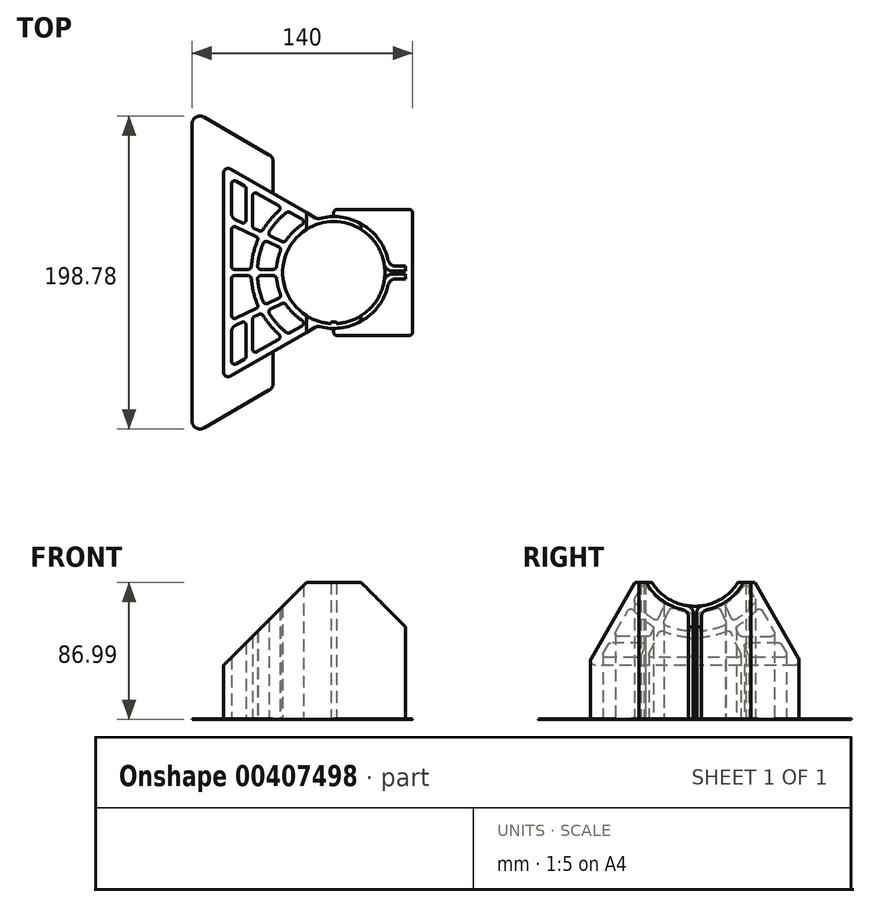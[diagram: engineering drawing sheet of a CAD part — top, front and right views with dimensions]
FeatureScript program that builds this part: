
annotation { "Feature Type Name" : "Feature", "Feature Type Description" : "" }
export const myFeature = defineFeature(function(context is Context, id is Id, definition is map)
    precondition{}
    {
        {
            var Q0;
            Q0=qCreatedBy(makeId("Top.planeOp"),FACE);
            var sketch = newSketch(context, id + "F0", { "sketchPlane" : qUnion([Q0])});
            skArc(sketch, "E0", {"start": v(32.08, 5.2) * mm, "mid": v(-24.03, 21.88) * mm, "end": v(-2.18, -32.43) * mm});
            skArc(sketch, "E1", {"start": v(34.61, 7.89) * mm, "mid": v(18.34, 30.4) * mm, "end": v(-9.16, 34.3) * mm});
            skLineSegment(sketch, "E2", {"start": v(39.49, 4) * mm, "end": v(45.5, 4) * mm});
            skLineSegment(sketch, "E3", {"start": v(39.49, -4) * mm, "end": v(45.5, -4) * mm});
            skLineSegment(sketch, "E4.0", {"start": v(37.02, 1) * mm, "end": v(45.5, 1) * mm});
            skLineSegment(sketch, "E5.0", {"start": v(37.02, -1) * mm, "end": v(45.5, -1) * mm});
            skLineSegment(sketch, "E6", {"start": v(45.5, 4) * mm, "end": v(45.5, 1) * mm});
            skLineSegment(sketch, "E7.trimOffspring", {"start": v(45.5, -1) * mm, "end": v(45.5, -4) * mm});
            skPoint(sketch, "E8.visualSharp", {"position": v(35.27, 4) * mm});
            skArc(sketch, "E8.filletArc", {"start": v(34.61, 7.89) * mm, "mid": v(36.37, 5.1) * mm, "end": v(39.49, 4) * mm});
            skPoint(sketch, "E9.visualSharp", {"position": v(35.27, -4) * mm});
            skArc(sketch, "E9.filletArc", {"start": v(39.49, -4) * mm, "mid": v(36.37, -5.1) * mm, "end": v(34.61, -7.89) * mm});
            skPoint(sketch, "E10.visualSharp", {"position": v(32.48, -1) * mm});
            skArc(sketch, "E10.filletArc", {"start": v(37.02, -1) * mm, "mid": v(33.78, -2.2) * mm, "end": v(32.08, -5.2) * mm});
            skPoint(sketch, "E11.visualSharp", {"position": v(32.48, 1) * mm});
            skArc(sketch, "E11.filletArc", {"start": v(32.08, 5.2) * mm, "mid": v(33.78, 2.2) * mm, "end": v(37.02, 1) * mm});
            skArc(sketch, "E12.trimOffspring", {"start": v(-9.16, -34.3) * mm, "mid": v(18.34, -30.4) * mm, "end": v(34.61, -7.89) * mm});
            skLineSegment(sketch, "E13", {"start": v(-11.44, 34.6) * mm, "end": v(-65.5, 65.81) * mm});
            skLineSegment(sketch, "E14", {"start": v(-11.44, -34.6) * mm, "end": v(-65.5, -65.81) * mm});
            skLineSegment(sketch, "E15", {"start": v(-70, 63.21) * mm, "end": v(-70, -63.21) * mm});
            skPoint(sketch, "E16.visualSharp", {"position": v(-70, 68.4) * mm});
            skArc(sketch, "E16.filletArc", {"start": v(-65.5, 65.81) * mm, "mid": v(-68.5, 65.81) * mm, "end": v(-70, 63.21) * mm});
            skPoint(sketch, "E17.visualSharp", {"position": v(-70, -68.4) * mm});
            skArc(sketch, "E17.filletArc", {"start": v(-70, -63.21) * mm, "mid": v(-68.5, -65.81) * mm, "end": v(-65.5, -65.81) * mm});
            skPoint(sketch, "E18.visualSharp", {"position": v(-10.34, 33.96) * mm});
            skArc(sketch, "E18.filletArc", {"start": v(-11.44, 34.6) * mm, "mid": v(-10.33, 34.22) * mm, "end": v(-9.16, 34.3) * mm});
            skPoint(sketch, "E19.visualSharp", {"position": v(-10.34, -33.96) * mm});
            skArc(sketch, "E19.filletArc", {"start": v(-9.16, -34.3) * mm, "mid": v(-10.33, -34.22) * mm, "end": v(-11.44, -34.6) * mm});
            skLineSegment(sketch, "E20.bottom", {"start": v(-1.35, -31.5) * mm, "end": v(1.35, -31.5) * mm});
            skLineSegment(sketch, "E20.left", {"start": v(-1.75, -31.9) * mm, "end": v(-1.75, -32.03) * mm});
            skLineSegment(sketch, "E20.right", {"start": v(1.75, -31.9) * mm, "end": v(1.75, -32.03) * mm});
            skArc(sketch, "E21.trimOffspring", {"start": v(2.18, -32.43) * mm, "mid": v(21.88, -24.03) * mm, "end": v(32.08, -5.2) * mm});
            skPoint(sketch, "E20.top.end.orphan", {"position": v(1.75, -33.96) * mm});
            skPoint(sketch, "E22.visualSharp", {"position": v(-1.75, -31.5) * mm});
            skArc(sketch, "E22.filletArc", {"start": v(-1.35, -31.5) * mm, "mid": v(-1.63, -31.62) * mm, "end": v(-1.75, -31.9) * mm});
            skPoint(sketch, "E23.visualSharp", {"position": v(1.75, -31.5) * mm});
            skArc(sketch, "E23.filletArc", {"start": v(1.75, -31.9) * mm, "mid": v(1.63, -31.62) * mm, "end": v(1.35, -31.5) * mm});
            skPoint(sketch, "E24.visualSharp", {"position": v(-1.75, -32.45) * mm});
            skArc(sketch, "E24.filletArc", {"start": v(-2.18, -32.43) * mm, "mid": v(-1.88, -32.32) * mm, "end": v(-1.75, -32.03) * mm});
            skPoint(sketch, "E25.visualSharp", {"position": v(1.75, -32.45) * mm});
            skArc(sketch, "E25.filletArc", {"start": v(1.75, -32.03) * mm, "mid": v(1.88, -32.32) * mm, "end": v(2.18, -32.43) * mm});
            skSolve(sketch);
        }
        {
            var Q0;
            Q0 = qSketchRegion(id + "F0", true);
            extrude(context, id + "F1", {"entities" : qUnion([Q0]), "depth" : 150 * mm});
        }
        {
            var Q0;
            Q0=qCreatedBy(makeId("Front.planeOp"),FACE);
            var sketch = newSketch(context, id + "F2", { "sketchPlane" : qUnion([Q0])});
            skLineSegment(sketch, "E26", {"start": v(-17.41, 86.99) * mm, "end": v(-77.36, 27.04) * mm});
            skLineSegment(sketch, "E27", {"start": v(50.55, 154.95) * mm, "end": v(-77.36, 154.95) * mm});
            skLineSegment(sketch, "E28", {"start": v(-77.36, 27.04) * mm, "end": v(-77.36, 154.95) * mm});
            skLineSegment(sketch, "E29", {"start": v(0, -24.5) * mm, "end": v(0, 134.81) * mm, "construction": true});
            skLineSegment(sketch, "E30", {"start": v(17.41, 86.99) * mm, "end": v(50.55, 53.86) * mm});
            skLineSegment(sketch, "E31", {"start": v(50.55, 154.95) * mm, "end": v(50.55, 53.86) * mm});
            skPoint(sketch, "E32.startSnap0", {"position": v(-77.36, 91) * mm});
            skPoint(sketch, "E33.orphan", {"position": v(-42.6, 91) * mm});
            skLineSegment(sketch, "E34", {"start": v(17.41, 86.99) * mm, "end": v(-17.41, 86.99) * mm});
            skSolve(sketch);
        }
        {
            var Q0;
            Q0 = qSketchRegion(id + "F2", true);
            extrude(context, id + "F3", {"entities" : qUnion([Q0]), "operationType" : NewBodyOperationType.REMOVE, "endBound" : BoundingType.SYMMETRIC, "oppositeDirection" : true, "depth" : 150 * mm});
        }
        {
            var Q0;
            Q0=qCreatedBy(makeId("Top.planeOp"),FACE);
            var sketch = newSketch(context, id + "F4", { "sketchPlane" : qUnion([Q0])});
            skLineSegment(sketch, "E35.bottom", {"start": v(2, -40) * mm, "end": v(48, -40) * mm});
            skLineSegment(sketch, "E35.top", {"start": v(2, 40) * mm, "end": v(48, 40) * mm});
            skLineSegment(sketch, "E35.left", {"start": v(0, -38) * mm, "end": v(0, -32.5) * mm});
            skLineSegment(sketch, "E35.right", {"start": v(50, -38) * mm, "end": v(50, 38) * mm});
            skPoint(sketch, "E36.visualSharp", {"position": v(0, -40) * mm});
            skArc(sketch, "E36.filletArc", {"start": v(0, -38) * mm, "mid": v(0.59, -39.41) * mm, "end": v(2, -40) * mm});
            skPoint(sketch, "E37.visualSharp", {"position": v(50, -40) * mm});
            skArc(sketch, "E37.filletArc", {"start": v(48, -40) * mm, "mid": v(49.41, -39.41) * mm, "end": v(50, -38) * mm});
            skPoint(sketch, "E38.visualSharp", {"position": v(50, 40) * mm});
            skArc(sketch, "E38.filletArc", {"start": v(50, 38) * mm, "mid": v(49.41, 39.41) * mm, "end": v(48, 40) * mm});
            skPoint(sketch, "E39.visualSharp", {"position": v(0, 40) * mm});
            skArc(sketch, "E39.filletArc", {"start": v(2, 40) * mm, "mid": v(0.59, 39.41) * mm, "end": v(0, 38) * mm});
            skArc(sketch, "E40", {"start": v(0, -32.5) * mm, "mid": v(32.5, 0) * mm, "end": v(0, 32.5) * mm});
            skLineSegment(sketch, "E41.trimOffspring", {"start": v(0, 32.5) * mm, "end": v(0, 38) * mm});
            skLineSegment(sketch, "E42", {"start": v(32.44, 2) * mm, "end": v(42.77, 2) * mm});
            skLineSegment(sketch, "E43", {"start": v(32.2, -4.38) * mm, "end": v(34.91, -4.38) * mm});
            skSolve(sketch);
        }
        {
            var Q0;
            Q0 = qSketchRegion(id + "F4", true);
            extrude(context, id + "F5", {"entities" : qUnion([Q0]), "operationType" : NewBodyOperationType.ADD, "depth" : 0.5 * mm});
        }
        {
            var Q0;
            Q0=makeQuery(id+"F5.boolean.opBoolean","MERGE",FACE,{"derivedFrom":[makeQuery(id+"F1.opExtrude","CAP_FACE",FACE,{"disambiguationData":[OSD([sQuery(id+"F0.wireOp",EDGE,"E0"),sQuery(id+"F0.wireOp",EDGE,"E1"),sQuery(id+"F0.wireOp",EDGE,"E2"),sQuery(id+"F0.wireOp",EDGE,"E3"),sQuery(id+"F0.wireOp",EDGE,"E4.0"),sQuery(id+"F0.wireOp",EDGE,"E5.0"),sQuery(id+"F0.wireOp",EDGE,"E6"),sQuery(id+"F0.wireOp",EDGE,"E7.trimOffspring"),sQuery(id+"F0.wireOp",EDGE,"E8.filletArc"),sQuery(id+"F0.wireOp",EDGE,"E9.filletArc"),sQuery(id+"F0.wireOp",EDGE,"E10.filletArc"),sQuery(id+"F0.wireOp",EDGE,"E11.filletArc"),sQuery(id+"F0.wireOp",EDGE,"E12.trimOffspring"),sQuery(id+"F0.wireOp",EDGE,"E13"),sQuery(id+"F0.wireOp",EDGE,"E14"),sQuery(id+"F0.wireOp",EDGE,"E15"),sQuery(id+"F0.wireOp",EDGE,"E16.filletArc"),sQuery(id+"F0.wireOp",EDGE,"E17.filletArc"),sQuery(id+"F0.wireOp",EDGE,"E18.filletArc"),sQuery(id+"F0.wireOp",EDGE,"E19.filletArc"),sQuery(id+"F0.wireOp",EDGE,"E20.bottom"),sQuery(id+"F0.wireOp",EDGE,"E20.left"),sQuery(id+"F0.wireOp",EDGE,"E20.right"),sQuery(id+"F0.wireOp",EDGE,"E21.trimOffspring"),sQuery(id+"F0.wireOp",EDGE,"E22.filletArc"),sQuery(id+"F0.wireOp",EDGE,"E23.filletArc"),sQuery(id+"F0.wireOp",EDGE,"E24.filletArc"),sQuery(id+"F0.wireOp",EDGE,"E25.filletArc")])],"isStart":true}),makeQuery(id+"F5.opExtrude","CAP_FACE",FACE,{"disambiguationData":[OSD([sQuery(id+"F4.wireOp",EDGE,"E35.bottom"),sQuery(id+"F4.wireOp",EDGE,"E35.top"),sQuery(id+"F4.wireOp",EDGE,"E35.left"),sQuery(id+"F4.wireOp",EDGE,"E35.right"),sQuery(id+"F4.wireOp",EDGE,"E36.filletArc"),sQuery(id+"F4.wireOp",EDGE,"E37.filletArc"),sQuery(id+"F4.wireOp",EDGE,"E38.filletArc"),sQuery(id+"F4.wireOp",EDGE,"E39.filletArc")])],"isStart":true})]});
            var sketch = newSketch(context, id + "F6", { "sketchPlane" : qUnion([Q0])});
            skLineSegment(sketch, "E44.9", {"start": v(-20.19, 33.88) * mm, "end": v(-27.78, 38.26) * mm});
            skLineSegment(sketch, "E44.10", {"start": v(-65, 56.28) * mm, "end": v(-65, 37.9) * mm});
            skLineSegment(sketch, "E44.11", {"start": v(-62, -58.02) * mm, "end": v(-56.63, -54.92) * mm});
            skArc(sketch, "E45.0", {"start": v(-20.09, -30.48) * mm, "mid": v(-25.68, -25.94) * mm, "end": v(-30.27, -20.4) * mm});
            skPoint(sketch, "E46.visualSharp", {"position": v(-65, 59.75) * mm});
            skArc(sketch, "E46.filletArc", {"start": v(-62, 58.02) * mm, "mid": v(-64, 58.02) * mm, "end": v(-65, 56.28) * mm});
            skPoint(sketch, "E47.visualSharp", {"position": v(-65, -59.75) * mm});
            skArc(sketch, "E47.filletArc", {"start": v(-65, -56.28) * mm, "mid": v(-64, -58.02) * mm, "end": v(-62, -58.02) * mm});
            skPoint(sketch, "E48.visualSharp", {"position": v(-17.24, -32.17) * mm});
            skArc(sketch, "E48.filletArc", {"start": v(-20.19, -33.88) * mm, "mid": v(-19.19, -32.2) * mm, "end": v(-20.09, -30.48) * mm});
            skPoint(sketch, "E49.visualSharp", {"position": v(-17.24, 32.17) * mm});
            skArc(sketch, "E49.filletArc", {"start": v(-20.09, 30.48) * mm, "mid": v(-19.19, 32.2) * mm, "end": v(-20.19, 33.88) * mm});
            skLineSegment(sketch, "E50", {"start": v(-63, 2) * mm, "end": v(-54.35, 2) * mm});
            skLineSegment(sketch, "E51", {"start": v(-63, -2) * mm, "end": v(-54.35, -2) * mm});
            skLineSegment(sketch, "E52.trimOffspring", {"start": v(-65, -4) * mm, "end": v(-65, -27.17) * mm});
            skArc(sketch, "E53.trimOffspring", {"start": v(-36.3, 3.8) * mm, "mid": v(-35.42, 8.83) * mm, "end": v(-33.84, 13.69) * mm});
            skPoint(sketch, "E54.visualSharp", {"position": v(-36.45, 2) * mm});
            skArc(sketch, "E54.filletArc", {"start": v(-38.3, 2) * mm, "mid": v(-36.95, 2.51) * mm, "end": v(-36.3, 3.8) * mm});
            skPoint(sketch, "E55.visualSharp", {"position": v(-36.45, -2) * mm});
            skArc(sketch, "E55.filletArc", {"start": v(-36.3, -3.8) * mm, "mid": v(-36.95, -2.51) * mm, "end": v(-38.3, -2) * mm});
            skPoint(sketch, "E56.visualSharp", {"position": v(-65, 2) * mm});
            skArc(sketch, "E56.filletArc", {"start": v(-65, 4) * mm, "mid": v(-64.41, 2.59) * mm, "end": v(-63, 2) * mm});
            skPoint(sketch, "E57.visualSharp", {"position": v(-65, -2) * mm});
            skArc(sketch, "E57.filletArc", {"start": v(-63, -2) * mm, "mid": v(-64.41, -2.59) * mm, "end": v(-65, -4) * mm});
            skLineSegment(sketch, "E58", {"start": v(-34.85, -16.25) * mm, "end": v(-42.1, -19.63) * mm});
            skLineSegment(sketch, "E59.0", {"start": v(-32.78, 19.7) * mm, "end": v(-40.1, 23.11) * mm});
            skLineSegment(sketch, "E60.0", {"start": v(-32.78, -19.7) * mm, "end": v(-40.1, -23.11) * mm});
            skLineSegment(sketch, "E61", {"start": v(-34.85, 16.25) * mm, "end": v(-42.1, 19.63) * mm});
            skLineSegment(sketch, "E62.trimOffspring", {"start": v(-65, 27.17) * mm, "end": v(-65, 4) * mm});
            skLineSegment(sketch, "E63.trimOffspring", {"start": v(-65, -37.9) * mm, "end": v(-65, -56.28) * mm});
            skArc(sketch, "E64.trimOffspring", {"start": v(-33.84, -13.69) * mm, "mid": v(-35.42, -8.83) * mm, "end": v(-36.3, -3.8) * mm});
            skArc(sketch, "E65.trimOffspring", {"start": v(-30.27, 20.4) * mm, "mid": v(-25.68, 25.94) * mm, "end": v(-20.09, 30.48) * mm});
            skPoint(sketch, "E66.visualSharp", {"position": v(-65, 34.72) * mm});
            skArc(sketch, "E66.filletArc", {"start": v(-65, 37.9) * mm, "mid": v(-64.22, 35.22) * mm, "end": v(-62.11, 33.38) * mm});
            skPoint(sketch, "E67.visualSharp", {"position": v(-65, -34.72) * mm});
            skArc(sketch, "E67.filletArc", {"start": v(-62.11, -33.38) * mm, "mid": v(-64.22, -35.22) * mm, "end": v(-65, -37.9) * mm});
            skPoint(sketch, "E68.visualSharp", {"position": v(-31.2, 18.96) * mm});
            skArc(sketch, "E68.filletArc", {"start": v(-32.78, 19.7) * mm, "mid": v(-31.4, 19.58) * mm, "end": v(-30.27, 20.4) * mm});
            skPoint(sketch, "E69.visualSharp", {"position": v(-31.2, -18.96) * mm});
            skArc(sketch, "E69.filletArc", {"start": v(-30.27, -20.4) * mm, "mid": v(-31.4, -19.58) * mm, "end": v(-32.78, -19.7) * mm});
            skPoint(sketch, "E70.visualSharp", {"position": v(-33.08, -15.43) * mm});
            skArc(sketch, "E70.filletArc", {"start": v(-34.85, -16.25) * mm, "mid": v(-33.83, -15.17) * mm, "end": v(-33.84, -13.69) * mm});
            skPoint(sketch, "E71.visualSharp", {"position": v(-33.08, 15.43) * mm});
            skArc(sketch, "E71.filletArc", {"start": v(-33.84, 13.69) * mm, "mid": v(-33.83, 15.17) * mm, "end": v(-34.85, 16.25) * mm});
            skPoint(sketch, "E72.visualSharp", {"position": v(-65, 30.3) * mm});
            skArc(sketch, "E72.filletArc", {"start": v(-62.15, 28.98) * mm, "mid": v(-64.07, 28.86) * mm, "end": v(-65, 27.17) * mm});
            skPoint(sketch, "E73.visualSharp", {"position": v(-65, -30.3) * mm});
            skArc(sketch, "E73.filletArc", {"start": v(-65, -27.17) * mm, "mid": v(-64.07, -28.86) * mm, "end": v(-62.15, -28.98) * mm});
            skArc(sketch, "E74.0", {"start": v(-34.82, -39.29) * mm, "mid": v(-40.29, -33.66) * mm, "end": v(-44.85, -27.3) * mm});
            skArc(sketch, "E75.0", {"start": v(-30.01, -38.1) * mm, "mid": v(-36, -32.5) * mm, "end": v(-40.94, -26) * mm});
            skArc(sketch, "E76.trimOffspring", {"start": v(-44.8, -18.59) * mm, "mid": v(-47.11, -11.52) * mm, "end": v(-48.32, -4.17) * mm});
            skArc(sketch, "E77.trimOffspring", {"start": v(-48.36, -20.43) * mm, "mid": v(-51.04, -12.3) * mm, "end": v(-52.36, -3.85) * mm});
            skLineSegment(sketch, "E78.trimOffspring", {"start": v(-47.4, -26.52) * mm, "end": v(-50.48, -27.95) * mm});
            skLineSegment(sketch, "E79.trimOffspring", {"start": v(-49.36, -23.02) * mm, "end": v(-62.15, -28.98) * mm});
            skLineSegment(sketch, "E80.trimOffspring", {"start": v(-47.4, 26.52) * mm, "end": v(-50.48, 27.95) * mm});
            skLineSegment(sketch, "E81.trimOffspring", {"start": v(-49.36, 23.02) * mm, "end": v(-62.15, 28.98) * mm});
            skArc(sketch, "E82.trimOffspring", {"start": v(-44.85, 27.3) * mm, "mid": v(-40.29, 33.66) * mm, "end": v(-34.82, 39.29) * mm});
            skArc(sketch, "E83.trimOffspring", {"start": v(-40.94, 26) * mm, "mid": v(-36, 32.5) * mm, "end": v(-30.01, 38.1) * mm});
            skLineSegment(sketch, "E84.trimOffspring", {"start": v(-35.15, 42.52) * mm, "end": v(-48.63, 50.3) * mm});
            skLineSegment(sketch, "E85.trimOffspring", {"start": v(-27.78, -38.26) * mm, "end": v(-20.19, -33.88) * mm});
            skLineSegment(sketch, "E86.trimOffspring", {"start": v(-46.33, 2) * mm, "end": v(-38.3, 2) * mm});
            skArc(sketch, "E87.trimOffspring", {"start": v(-52.36, 3.85) * mm, "mid": v(-51.04, 12.3) * mm, "end": v(-48.36, 20.43) * mm});
            skArc(sketch, "E88.trimOffspring", {"start": v(-48.32, 4.17) * mm, "mid": v(-47.11, 11.52) * mm, "end": v(-44.8, 18.59) * mm});
            skLineSegment(sketch, "E89.trimOffspring", {"start": v(-46.33, -2) * mm, "end": v(-38.3, -2) * mm});
            skLineSegment(sketch, "E90", {"start": v(-55.63, 53.19) * mm, "end": v(-55.63, 33.5) * mm});
            skLineSegment(sketch, "E91", {"start": v(-51.63, -48.57) * mm, "end": v(-51.63, -29.77) * mm});
            skLineSegment(sketch, "E92", {"start": v(-51.63, 48.57) * mm, "end": v(-51.63, 29.77) * mm});
            skLineSegment(sketch, "E93.trimOffspring", {"start": v(-55.63, -33.5) * mm, "end": v(-55.63, -53.19) * mm});
            skLineSegment(sketch, "E94.trimOffspring", {"start": v(-58.48, -31.68) * mm, "end": v(-62.11, -33.38) * mm});
            skLineSegment(sketch, "E95.trimOffspring", {"start": v(-48.63, -50.3) * mm, "end": v(-35.15, -42.52) * mm});
            skLineSegment(sketch, "E96.trimOffspring", {"start": v(-58.48, 31.68) * mm, "end": v(-62.11, 33.38) * mm});
            skLineSegment(sketch, "E97.trimOffspring", {"start": v(-56.63, 54.92) * mm, "end": v(-62, 58.02) * mm});
            skPoint(sketch, "E98.visualSharp", {"position": v(-51.63, 52.03) * mm});
            skArc(sketch, "E98.filletArc", {"start": v(-48.63, 50.3) * mm, "mid": v(-50.63, 50.3) * mm, "end": v(-51.63, 48.57) * mm});
            skPoint(sketch, "E99.visualSharp", {"position": v(-55.63, 54.34) * mm});
            skArc(sketch, "E99.filletArc", {"start": v(-55.63, 53.19) * mm, "mid": v(-55.9, 54.19) * mm, "end": v(-56.63, 54.92) * mm});
            skPoint(sketch, "E100.visualSharp", {"position": v(-51.63, -52.03) * mm});
            skArc(sketch, "E100.filletArc", {"start": v(-51.63, -48.57) * mm, "mid": v(-50.63, -50.3) * mm, "end": v(-48.63, -50.3) * mm});
            skPoint(sketch, "E101.visualSharp", {"position": v(-55.63, -54.34) * mm});
            skArc(sketch, "E101.filletArc", {"start": v(-56.63, -54.92) * mm, "mid": v(-55.9, -54.19) * mm, "end": v(-55.63, -53.19) * mm});
            skPoint(sketch, "E102.visualSharp", {"position": v(-51.63, -28.5) * mm});
            skArc(sketch, "E102.filletArc", {"start": v(-50.48, -27.95) * mm, "mid": v(-51.32, -28.7) * mm, "end": v(-51.63, -29.77) * mm});
            skPoint(sketch, "E103.visualSharp", {"position": v(-55.63, -30.36) * mm});
            skArc(sketch, "E103.filletArc", {"start": v(-55.63, -33.5) * mm, "mid": v(-56.56, -31.8) * mm, "end": v(-58.48, -31.68) * mm});
            skPoint(sketch, "E104.visualSharp", {"position": v(-55.63, 30.36) * mm});
            skArc(sketch, "E104.filletArc", {"start": v(-58.48, 31.68) * mm, "mid": v(-56.56, 31.8) * mm, "end": v(-55.63, 33.5) * mm});
            skPoint(sketch, "E105.visualSharp", {"position": v(-51.63, 28.5) * mm});
            skArc(sketch, "E105.filletArc", {"start": v(-51.63, 29.77) * mm, "mid": v(-51.32, 28.7) * mm, "end": v(-50.48, 27.95) * mm});
            skPoint(sketch, "E106.visualSharp", {"position": v(-47.58, 22.19) * mm});
            skArc(sketch, "E106.filletArc", {"start": v(-48.36, 20.43) * mm, "mid": v(-48.34, 21.92) * mm, "end": v(-49.36, 23.02) * mm});
            skPoint(sketch, "E107.visualSharp", {"position": v(-52.46, 2) * mm});
            skArc(sketch, "E107.filletArc", {"start": v(-54.35, 2) * mm, "mid": v(-53, 2.53) * mm, "end": v(-52.36, 3.85) * mm});
            skPoint(sketch, "E108.visualSharp", {"position": v(-52.46, -2) * mm});
            skArc(sketch, "E108.filletArc", {"start": v(-52.36, -3.85) * mm, "mid": v(-53, -2.53) * mm, "end": v(-54.35, -2) * mm});
            skPoint(sketch, "E109.visualSharp", {"position": v(-47.58, -22.19) * mm});
            skArc(sketch, "E109.filletArc", {"start": v(-49.36, -23.02) * mm, "mid": v(-48.34, -21.92) * mm, "end": v(-48.36, -20.43) * mm});
            skPoint(sketch, "E110.visualSharp", {"position": v(-45.75, -25.75) * mm});
            skArc(sketch, "E110.filletArc", {"start": v(-44.85, -27.3) * mm, "mid": v(-45.98, -26.42) * mm, "end": v(-47.4, -26.52) * mm});
            skPoint(sketch, "E111.visualSharp", {"position": v(-32.68, -41.09) * mm});
            skArc(sketch, "E111.filletArc", {"start": v(-35.15, -42.52) * mm, "mid": v(-34.16, -40.99) * mm, "end": v(-34.82, -39.29) * mm});
            skPoint(sketch, "E112.visualSharp", {"position": v(-28.93, -38.93) * mm});
            skArc(sketch, "E112.filletArc", {"start": v(-30.01, -38.1) * mm, "mid": v(-28.92, -38.52) * mm, "end": v(-27.78, -38.26) * mm});
            skPoint(sketch, "E113.visualSharp", {"position": v(-42.12, -24.05) * mm});
            skArc(sketch, "E113.filletArc", {"start": v(-40.1, -23.11) * mm, "mid": v(-41.17, -24.36) * mm, "end": v(-40.94, -26) * mm});
            skPoint(sketch, "E114.visualSharp", {"position": v(-43.96, -20.5) * mm});
            skArc(sketch, "E114.filletArc", {"start": v(-44.8, -18.59) * mm, "mid": v(-43.67, -19.69) * mm, "end": v(-42.1, -19.63) * mm});
            skPoint(sketch, "E115.visualSharp", {"position": v(-48.46, -2) * mm});
            skArc(sketch, "E115.filletArc", {"start": v(-46.33, -2) * mm, "mid": v(-47.8, -2.65) * mm, "end": v(-48.32, -4.17) * mm});
            skPoint(sketch, "E116.visualSharp", {"position": v(-48.46, 2) * mm});
            skArc(sketch, "E116.filletArc", {"start": v(-48.32, 4.17) * mm, "mid": v(-47.8, 2.65) * mm, "end": v(-46.33, 2) * mm});
            skPoint(sketch, "E117.visualSharp", {"position": v(-43.96, 20.5) * mm});
            skArc(sketch, "E117.filletArc", {"start": v(-42.1, 19.63) * mm, "mid": v(-43.67, 19.69) * mm, "end": v(-44.8, 18.59) * mm});
            skPoint(sketch, "E118.visualSharp", {"position": v(-42.12, 24.05) * mm});
            skArc(sketch, "E118.filletArc", {"start": v(-40.94, 26) * mm, "mid": v(-41.17, 24.36) * mm, "end": v(-40.1, 23.11) * mm});
            skPoint(sketch, "E119.visualSharp", {"position": v(-45.75, 25.75) * mm});
            skArc(sketch, "E119.filletArc", {"start": v(-47.4, 26.52) * mm, "mid": v(-45.98, 26.42) * mm, "end": v(-44.85, 27.3) * mm});
            skPoint(sketch, "E120.visualSharp", {"position": v(-28.93, 38.93) * mm});
            skArc(sketch, "E120.filletArc", {"start": v(-27.78, 38.26) * mm, "mid": v(-28.92, 38.52) * mm, "end": v(-30.01, 38.1) * mm});
            skPoint(sketch, "E121.visualSharp", {"position": v(-32.68, 41.09) * mm});
            skArc(sketch, "E121.filletArc", {"start": v(-34.82, 39.29) * mm, "mid": v(-34.16, 40.99) * mm, "end": v(-35.15, 42.52) * mm});
            skSolve(sketch);
        }
        {
            var Q0;
            Q0 = qSketchRegion(id + "F6", true);
            extrude(context, id + "F7", {"entities" : qUnion([Q0]), "operationType" : NewBodyOperationType.REMOVE, "endBound" : BoundingType.THROUGH_ALL, "oppositeDirection" : true, "depth" : 25 * mm});
        }
        {
            var Q0;
            Q0=makeQuery(id+"F5.boolean.opBoolean","MERGE",FACE,{"derivedFrom":[makeQuery(id+"F1.opExtrude","CAP_FACE",FACE,{"disambiguationData":[OSD([sQuery(id+"F0.wireOp",EDGE,"E0"),sQuery(id+"F0.wireOp",EDGE,"E1"),sQuery(id+"F0.wireOp",EDGE,"E2"),sQuery(id+"F0.wireOp",EDGE,"E3"),sQuery(id+"F0.wireOp",EDGE,"E4.0"),sQuery(id+"F0.wireOp",EDGE,"E5.0"),sQuery(id+"F0.wireOp",EDGE,"E6"),sQuery(id+"F0.wireOp",EDGE,"E7.trimOffspring"),sQuery(id+"F0.wireOp",EDGE,"E8.filletArc"),sQuery(id+"F0.wireOp",EDGE,"E9.filletArc"),sQuery(id+"F0.wireOp",EDGE,"E10.filletArc"),sQuery(id+"F0.wireOp",EDGE,"E11.filletArc"),sQuery(id+"F0.wireOp",EDGE,"E12.trimOffspring"),sQuery(id+"F0.wireOp",EDGE,"E13"),sQuery(id+"F0.wireOp",EDGE,"E14"),sQuery(id+"F0.wireOp",EDGE,"E15"),sQuery(id+"F0.wireOp",EDGE,"E16.filletArc"),sQuery(id+"F0.wireOp",EDGE,"E17.filletArc"),sQuery(id+"F0.wireOp",EDGE,"E18.filletArc"),sQuery(id+"F0.wireOp",EDGE,"E19.filletArc"),sQuery(id+"F0.wireOp",EDGE,"E20.bottom"),sQuery(id+"F0.wireOp",EDGE,"E20.left"),sQuery(id+"F0.wireOp",EDGE,"E20.right"),sQuery(id+"F0.wireOp",EDGE,"E21.trimOffspring"),sQuery(id+"F0.wireOp",EDGE,"E22.filletArc"),sQuery(id+"F0.wireOp",EDGE,"E23.filletArc"),sQuery(id+"F0.wireOp",EDGE,"E24.filletArc"),sQuery(id+"F0.wireOp",EDGE,"E25.filletArc")])],"isStart":true}),makeQuery(id+"F5.opExtrude","CAP_FACE",FACE,{"disambiguationData":[OSD([sQuery(id+"F4.wireOp",EDGE,"E35.bottom"),sQuery(id+"F4.wireOp",EDGE,"E35.top"),sQuery(id+"F4.wireOp",EDGE,"E35.left"),sQuery(id+"F4.wireOp",EDGE,"E35.right"),sQuery(id+"F4.wireOp",EDGE,"E36.filletArc"),sQuery(id+"F4.wireOp",EDGE,"E37.filletArc"),sQuery(id+"F4.wireOp",EDGE,"E38.filletArc"),sQuery(id+"F4.wireOp",EDGE,"E39.filletArc"),sQuery(id+"F4.wireOp",EDGE,"E40"),sQuery(id+"F4.wireOp",EDGE,"E41.trimOffspring")])],"isStart":true})]});
            var sketch = newSketch(context, id + "F8", { "sketchPlane" : qUnion([Q0])});
            skLineSegment(sketch, "E122", {"start": v(-38.47, 70.41) * mm, "end": v(-38.47, 47.1) * mm});
            skPoint(sketch, "E122.startSnap0", {"position": v(-38.47, 50.2) * mm});
            skLineSegment(sketch, "E123.0", {"start": v(-40.97, 74.74) * mm, "end": v(-82.5, 98.72) * mm});
            skLineSegment(sketch, "E124.0", {"start": v(-40.97, -74.74) * mm, "end": v(-82.5, -98.72) * mm});
            skLineSegment(sketch, "E125.0", {"start": v(-90, -94.39) * mm, "end": v(-90, 94.39) * mm});
            skPoint(sketch, "E126.orphan", {"position": v(-38.47, 94.21) * mm});
            skLineSegment(sketch, "E127", {"start": v(-38.47, 47.1) * mm, "end": v(-67, 63.21) * mm});
            skLineSegment(sketch, "E128", {"start": v(-67, 63.21) * mm, "end": v(-67, -63.21) * mm});
            skLineSegment(sketch, "E129", {"start": v(-67, -63.21) * mm, "end": v(-38.47, -46.74) * mm});
            skLineSegment(sketch, "E130.trimOffspring", {"start": v(-38.47, -46.74) * mm, "end": v(-38.47, -70.41) * mm});
            skPoint(sketch, "E131.visualSharp", {"position": v(-90, 103.05) * mm});
            skArc(sketch, "E131.filletArc", {"start": v(-82.5, 98.72) * mm, "mid": v(-87.5, 98.72) * mm, "end": v(-90, 94.39) * mm});
            skPoint(sketch, "E132.visualSharp", {"position": v(-90, -103.05) * mm});
            skArc(sketch, "E132.filletArc", {"start": v(-90, -94.39) * mm, "mid": v(-87.5, -98.72) * mm, "end": v(-82.5, -98.72) * mm});
            skPoint(sketch, "E133.visualSharp", {"position": v(-38.47, 73.3) * mm});
            skArc(sketch, "E133.filletArc", {"start": v(-38.47, 70.41) * mm, "mid": v(-39.14, 72.91) * mm, "end": v(-40.97, 74.74) * mm});
            skPoint(sketch, "E134.visualSharp", {"position": v(-38.47, -73.3) * mm});
            skArc(sketch, "E134.filletArc", {"start": v(-40.97, -74.74) * mm, "mid": v(-39.14, -72.91) * mm, "end": v(-38.47, -70.41) * mm});
            skSolve(sketch);
        }
        {
            var Q0;
            Q0=makeQuery(id+"F8.imprint","IMPRINT",FACE,{"disambiguationData":[TD([[makeQuery(id+"F8.imprint","IMPRINT",EDGE,{"derivedFrom":sQuery(id+"F8.wireOp",EDGE,"E123.0")}),1.0]])]});
            extrude(context, id + "F9", {"entities" : qUnion([Q0]), "operationType" : NewBodyOperationType.ADD, "oppositeDirection" : true, "depth" : .5 * mm});
        }
    });
